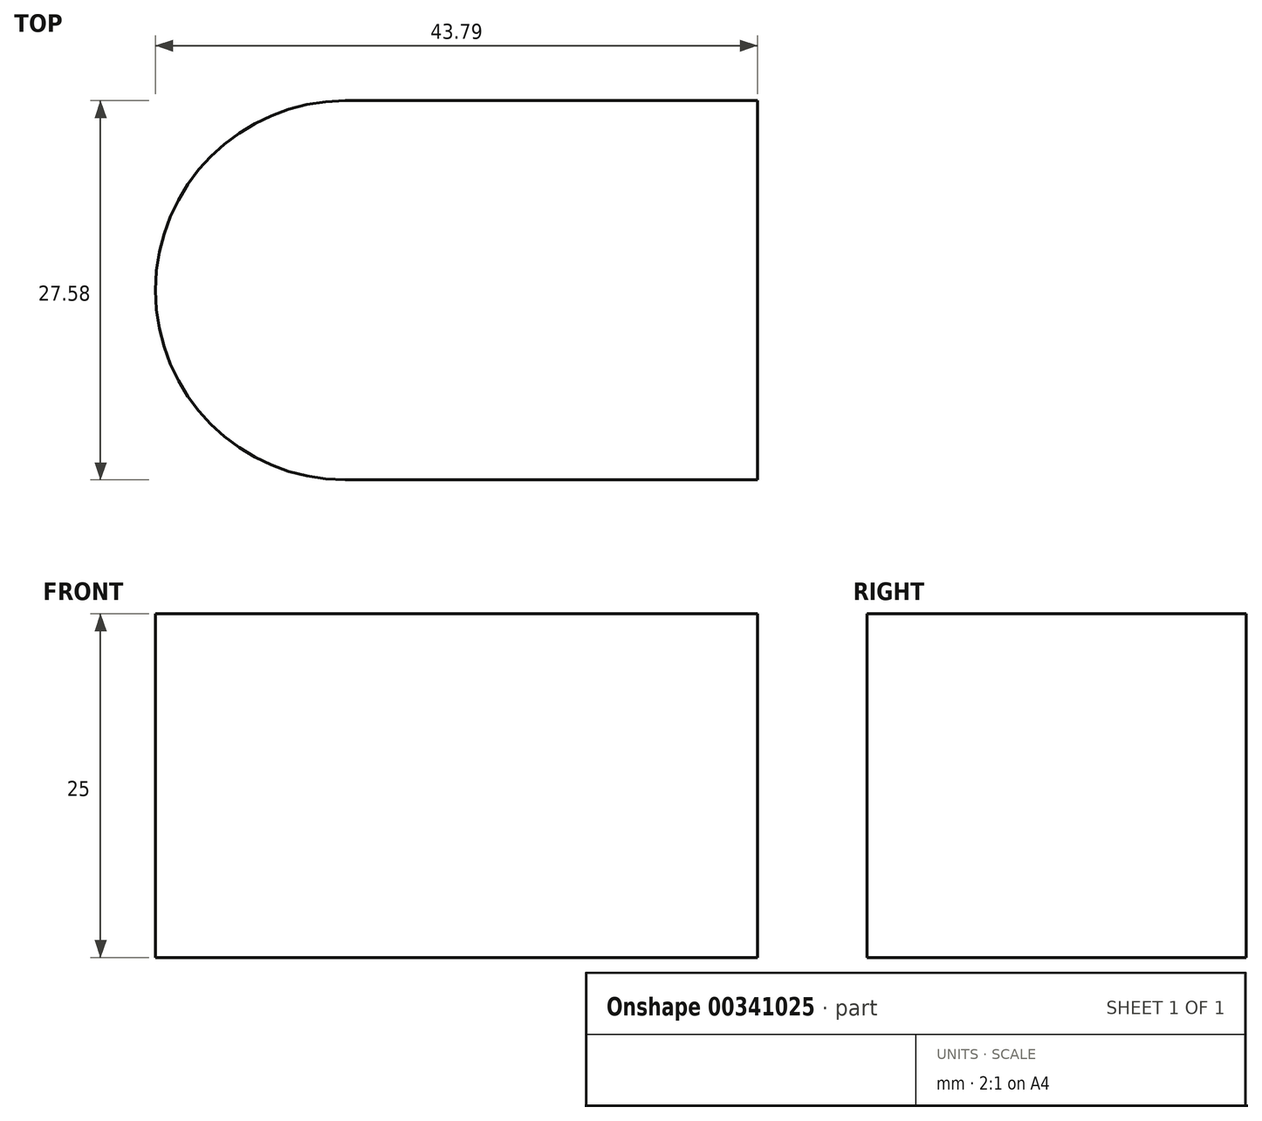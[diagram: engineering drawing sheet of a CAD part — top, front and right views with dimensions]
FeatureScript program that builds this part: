
annotation { "Feature Type Name" : "Feature", "Feature Type Description" : "" }
export const myFeature = defineFeature(function(context is Context, id is Id, definition is map)
    precondition{}
    {
        {
            var Q0;
            Q0=qCreatedBy(makeId("Top.planeOp"),FACE);
            var sketch = newSketch(context, id + "F0", { "sketchPlane" : qUnion([Q0])});
            skLineSegment(sketch, "E0.bottom", {"start": v(15, -13.8) * mm, "end": v(-15, -13.8) * mm});
            skLineSegment(sketch, "E0.top", {"start": v(15, 13.8) * mm, "end": v(-15, 13.8) * mm});
            skLineSegment(sketch, "E0.left", {"start": v(15, -13.8) * mm, "end": v(15, 13.8) * mm});
            skLineSegment(sketch, "E0.right", {"start": v(-15, -13.8) * mm, "end": v(-15, 13.8) * mm});
            skPoint(sketch, "E0.middle", {"position": v(0, 0) * mm});
            skCircle(sketch, "E1", {"center": v(-15, 0) * mm, "radius": 13.8 * mm});
            skSolve(sketch);
        }
        {
            var Q0;
            Q0 = qSketchRegion(id + "F0", true);
            extrude(context, id + "F1", {"entities" : qUnion([Q0]), "depth" : 25 * mm});
        }
    });
